# Revit family: Door-Sectional_DesignersChoice_Amarr
name_source: partatom
category: Doors
units: mm (PartAtom-declared; Revit-internal decimal feet)

## family parameters
Always vertical = Yes
Classification Number = 23.30.10.17.37.14
Cut with Voids When Loaded = No
Host = Wall
Room Calculation Point = No
Shared = No

## types (1)
- ByType
    21" Section Heights = Yes
    24" Section Heights = No
    Assembly Code = B2030410
    Construction Details = https://www.arcat.com
    Cost = 0 $
    Description = Door Sectional Designers Choice
    Door Cladding Material = Finishes - Exterior - White
    Door Gap From Wall Interior = 0' - 0 11/32"
    Door Open = Yes
    Door Track Material = Finishes - Exterior - White
    Fire Rating = As Specified in 08 36 00
    Function = Interior
    Green Building-LEED = https://www.arcat.com
    Has Operator = Yes
    Height = 10' - 0"
    Keynote = 08 36 00
    Manufacturer = Amarr Garage Doors
    Model = As Specified in 08 36 00
    Number of Sections = 4
    Operator Material = Finishes - Exterior - White
    Panel Width = 10' - 2"
    Product Data = http://www.arcat.com
    Rough Height = 0' - 0"
    Rough Width = 0' - 0"
    Section Heights = 1' - 9"
    Section Heights XX = 2' - 0"
    Specification = https://www.arcat.com
    Thickness = 0' - 2"
    Track Width = 10' - 3 9/16"
    Type Comments = ***Use image file as decal to display appropriate appearance
    URL = https://www.amarr.com
    Wall Closure = By host
    Width = 10' - 0"

## geometry (parser evidence)
native form markers: Blend x7, Sweep x18
no freeform markers — native parametric forms only
